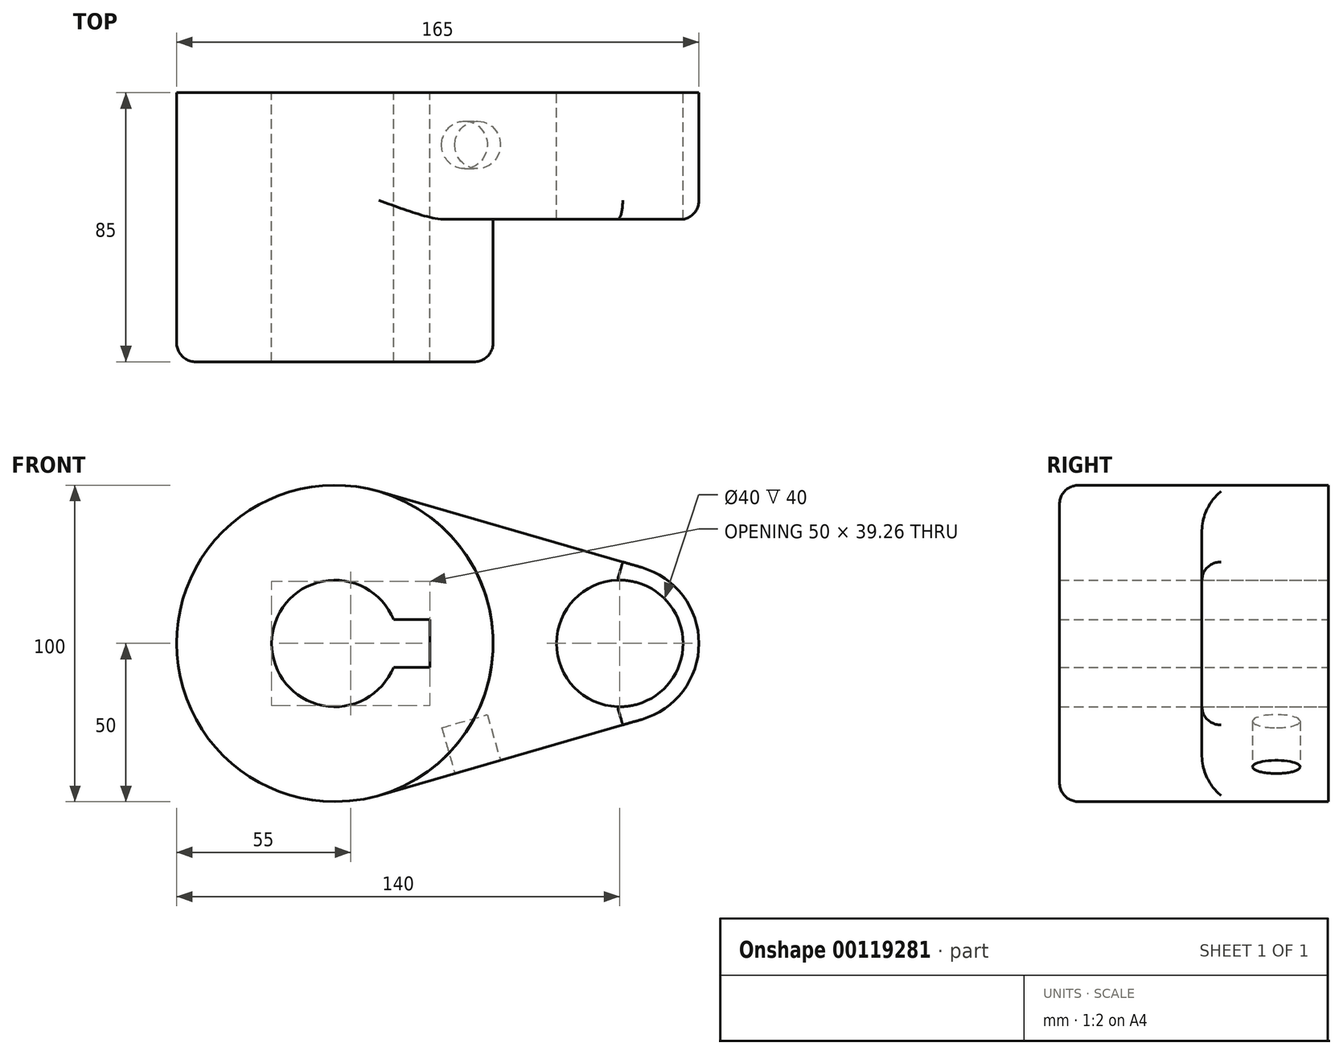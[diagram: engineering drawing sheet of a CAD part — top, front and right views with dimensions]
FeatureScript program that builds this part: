
annotation { "Feature Type Name" : "Feature", "Feature Type Description" : "" }
export const myFeature = defineFeature(function(context is Context, id is Id, definition is map)
    precondition{}
    {
        {
            var Q0;
            Q0=qCreatedBy(makeId("Front.planeOp"),FACE);
            var sketch = newSketch(context, id + "F0", { "sketchPlane" : qUnion([Q0])});
            skCircle(sketch, "E0", {"center": v(0, 0) * mm, "radius": 50 * mm});
            skCircle(sketch, "E1", {"center": v(90, 0) * mm, "radius": 25 * mm});
            skLineSegment(sketch, "E2", {"start": v(13.89, 48.03) * mm, "end": v(96.94, 24.02) * mm});
            skLineSegment(sketch, "E3", {"start": v(13.89, -48.03) * mm, "end": v(96.94, -24.02) * mm});
            skCircle(sketch, "E4", {"center": v(0, 0) * mm, "radius": 20 * mm});
            skCircle(sketch, "E5", {"center": v(90, 0) * mm, "radius": 20 * mm});
            skLineSegment(sketch, "E6.bottom", {"start": v(-30, 7.5) * mm, "end": v(30, 7.5) * mm});
            skLineSegment(sketch, "E6.top", {"start": v(-30, -7.5) * mm, "end": v(30, -7.5) * mm});
            skLineSegment(sketch, "E6.left", {"start": v(-30, 7.5) * mm, "end": v(-30, -7.5) * mm});
            skLineSegment(sketch, "E6.right", {"start": v(30, 7.5) * mm, "end": v(30, -7.5) * mm});
            skLineSegment(sketch, "E7", {"start": v(90, 0) * mm, "end": v(51.71, 0) * mm, "construction": true});
            skSolve(sketch);
        }
        {
            var Q0;
            {var subQ11=sQuery(id+"F0.wireOp",EDGE,"E6.left");Q0=makeQuery(id+"F0.imprint","IMPRINT",FACE,{"disambiguationData":[TD([[makeQuery(id+"F0.imprint","IMPRINT",EDGE,{"derivedFrom":subQ11}),-1.0]])]});}
            var Q1;
            {var subQ5=sQuery(id+"F0.wireOp",EDGE,"E6.left");Q1=makeQuery(id+"F0.imprint","IMPRINT",FACE,{"disambiguationData":[TD([[makeQuery(id+"F0.imprint","IMPRINT",EDGE,{"derivedFrom":subQ5}),1.0]])]});}
            var Q2;
            {var subQ0=sQuery(id+"F0.wireOp",EDGE,"E2");Q2=makeQuery(id+"F0.imprint","IMPRINT",FACE,{"disambiguationData":[TD([[makeQuery(id+"F0.imprint","IMPRINT",EDGE,{"derivedFrom":subQ0}),-1.0]])]});}
            var Q3;
            Q3=makeQuery(id+"F0.imprint","IMPRINT",FACE,{"disambiguationData":[TD([[makeQuery(id+"F0.imprint","IMPRINT",EDGE,{"derivedFrom":sQuery(id+"F0.wireOp",EDGE,"E5")}),-1.0]])]});
            extrude(context, id + "F1", {"entities" : qUnion([Q0, Q1, Q2, Q3]), "depth" : 40 * mm});
        }
        {
            var Q0;
            {var subQ11=sQuery(id+"F0.wireOp",EDGE,"E6.left");Q0=makeQuery(id+"F0.imprint","IMPRINT",FACE,{"disambiguationData":[TD([[makeQuery(id+"F0.imprint","IMPRINT",EDGE,{"derivedFrom":subQ11}),-1.0]])]});}
            var Q1;
            {var subQ5=sQuery(id+"F0.wireOp",EDGE,"E6.left");Q1=makeQuery(id+"F0.imprint","IMPRINT",FACE,{"disambiguationData":[TD([[makeQuery(id+"F0.imprint","IMPRINT",EDGE,{"derivedFrom":subQ5}),1.0]])]});}
            extrude(context, id + "F2", {"entities" : qUnion([Q0, Q1]), "operationType" : NewBodyOperationType.ADD, "depth" : 70 * mm});
        }
        {
            var Q0;
            Q0=makeQuery(id+"F2.opExtrude","CAP_FACE",FACE,{"disambiguationData":[OSD([sQuery(id+"F0.wireOp",EDGE,"E0"),sQuery(id+"F0.wireOp",EDGE,"E4"),sQuery(id+"F0.wireOp",EDGE,"E6.bottom"),sQuery(id+"F0.wireOp",EDGE,"E6.top"),sQuery(id+"F0.wireOp",EDGE,"E6.right")])],"isStart":false});
            extrude(context, id + "F3", {"entities" : qUnion([Q0]), "operationType" : NewBodyOperationType.ADD, "depth" : 15 * mm});
        }
        {
            var Q0;
            Q0=makeQuery(id+"F3.opExtrude","CAP_EDGE",EDGE,{"disambiguationData":[OSD([sQuery(id+"F0.wireOp",EDGE,"E0")])],"isStart":false});
            fillet(context, id + "F4", {"entities" : qUnion([Q0]), "radius" : 6 * mm, "tangentPropagation" : true, "allowEdgeOverflow" : false});
        }
        {
            var Q0;
            Q0=makeQuery(id+"F1.opExtrude","CAP_EDGE",EDGE,{"disambiguationData":[OSD([sQuery(id+"F0.wireOp",EDGE,"E1")])],"isStart":false});
            fillet(context, id + "F5", {"entities" : qUnion([Q0]), "radius" : 6 * mm, "tangentPropagation" : true, "allowEdgeOverflow" : false});
        }
        {
            var Q0;
            Q0=makeQuery(id+"F1.opExtrude","SWEPT_FACE",FACE,{"disambiguationData":[OSD([sQuery(id+"F0.wireOp",EDGE,"E3")])]});
            var sketch = newSketch(context, id + "F6", { "sketchPlane" : qUnion([Q0])});
            skCircle(sketch, "E8", {"center": v(38.44, 16.87) * mm, "radius": 5 * mm});
            skSolve(sketch);
        }
        {
            var Q0;
            Q0 = qSketchRegion(id + "F6", true);
            extrude(context, id + "F7", {"entities" : qUnion([Q0]), "operationType" : NewBodyOperationType.ADD, "oppositeDirection" : true, "depth" : 17.94 * mm});
        }
        {
            var Q0;
            Q0=makeQuery(id+"F1.opExtrude","SWEPT_FACE",FACE,{"disambiguationData":[OSD([sQuery(id+"F0.wireOp",EDGE,"E3")])]});
            var sketch = newSketch(context, id + "F8", { "sketchPlane" : qUnion([Q0])});
            skCircle(sketch, "E9", {"center": v(32.5, 16.5) * mm, "radius": 7.5 * mm});
            skSolve(sketch);
        }
        {
            var Q0;
            Q0 = qSketchRegion(id + "F8", true);
            extrude(context, id + "F9", {"entities" : qUnion([Q0]), "operationType" : NewBodyOperationType.REMOVE, "oppositeDirection" : true, "depth" : 15.02 * mm});
        }
    });
